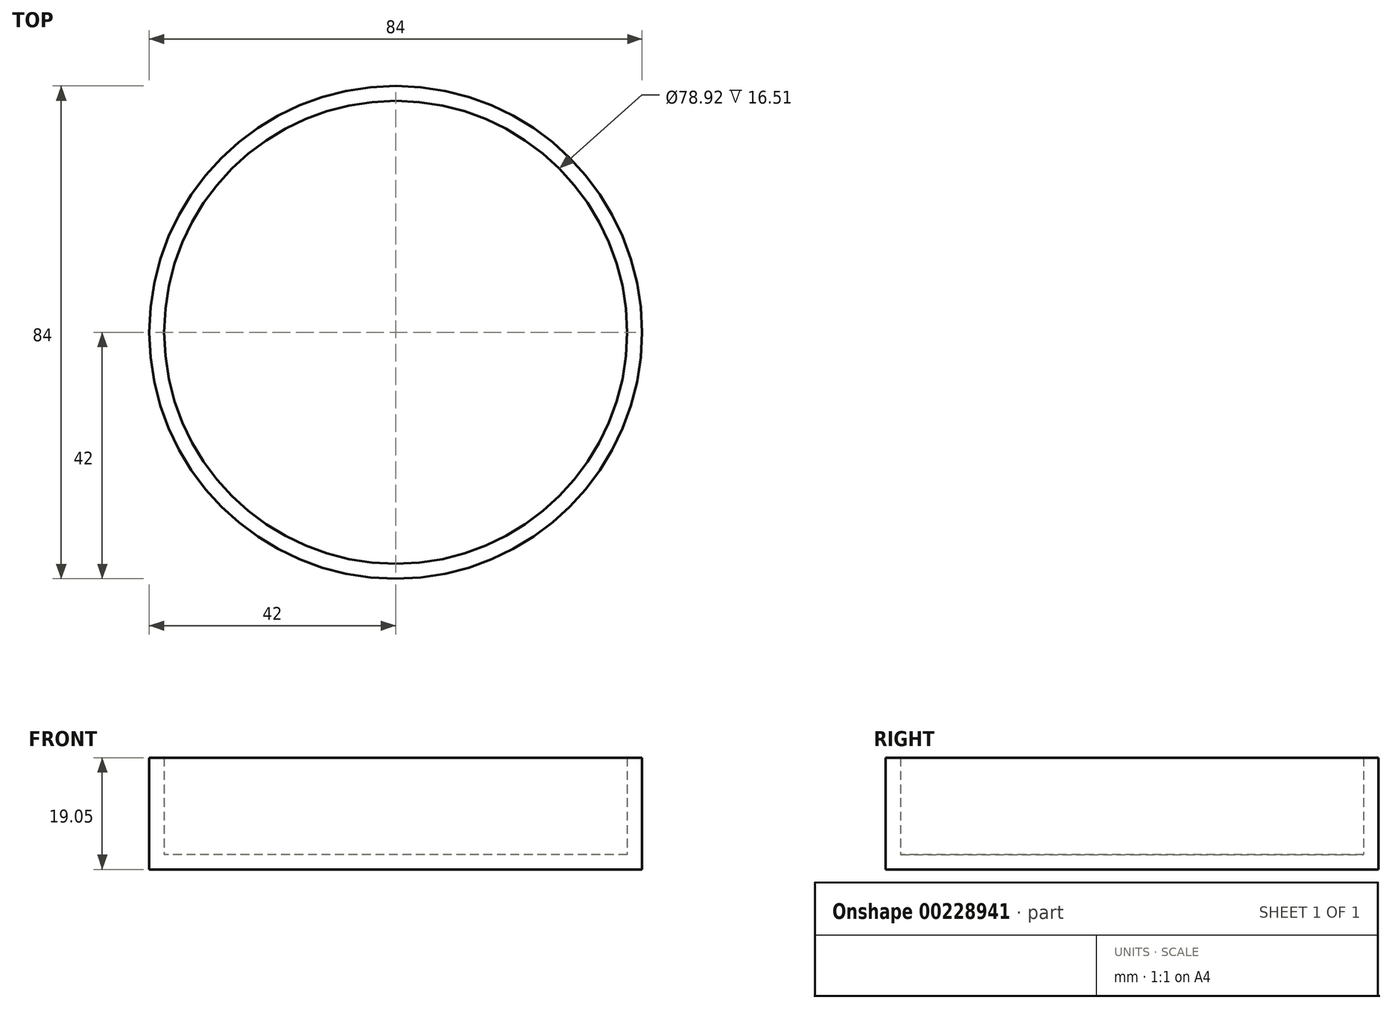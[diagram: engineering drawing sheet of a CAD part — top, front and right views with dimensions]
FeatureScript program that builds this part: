
annotation { "Feature Type Name" : "Feature", "Feature Type Description" : "" }
export const myFeature = defineFeature(function(context is Context, id is Id, definition is map)
    precondition{}
    {
        {
            var Q0;
            Q0=qCreatedBy(makeId("Top.planeOp"),FACE);
            var sketch = newSketch(context, id + "F0", { "sketchPlane" : qUnion([Q0])});
            skCircle(sketch, "E0", {"center": v(0, 0) * mm, "radius": 42 * mm});
            skSolve(sketch);
        }
        {
            var Q0;
            Q0 = qSketchRegion(id + "F0", true);
            extrude(context, id + "F1", {"entities" : qUnion([Q0]), "depth" : 19.05 * mm});
        }
        {
            var Q0;
            Q0 = qSketchRegion(id + "F0", true);
            extrude(context, id + "F2", {"entities" : qUnion([Q0]), "depth" : 3 / 101.6 * mm});
        }
        {
            var Q0;
            Q0=makeQuery(id+"F1.opExtrude","CAP_FACE",FACE,{"disambiguationData":[OSD([sQuery(id+"F0.wireOp",EDGE,"E0")])],"isStart":false});
            shell(context, id + "F3", {"entities" : qUnion([Q0]), "thickness" : 2.54 * mm});
        }
        {
            var Q0;
            Q0=makeQuery(id+"F2.opExtrude","SWEPT_BODY",BODY,{"disambiguationData":[OSD([sQuery(id+"F0.wireOp",EDGE,"E0")])]});
            deleteBodies(context, id + "F4", {"entities" : qUnion([Q0])});
        }
    });
